# Revit family: QSC TSC-70-G3 Stand
name_source: partatom
category: Communication Devices
revit_build: Autodesk Revit 2018 (Build: 20190510_1515(x64)
units: mm (PartAtom-declared; Revit-internal decimal feet)

## family parameters
Cut with Voids When Loaded = Yes
Host = Face
Maintain Annotation Orientation = No
Part Type = Normal
Room Calculation Point = No
Round Connector Dimension = Use Diameter
Shared = No

## types (1)
- QSC TSC-70-G3 Stand
    Communication Ports = 1 Gbps RJ45 LAN, 1 Type-C USB 3.1 (Future Use)
    Default Elevation = 0.0 mm
    Depth = 39.1 mm
    Description = PoE Touch Screen Controller
    Enclosure Material = Steel, Paint Finish, Dark Gray, Matte
    Face Material = Glossy Black
    Heat Load Active = 26
    Height = 115.0 mm
    Manufacturer = QSC, LLC
    Manufacturer URL = http://www.qsc.com
    Model = TSC-70-G3
    Product Documentation Link = https://www.qsc.com
    Product Page URL = https://www.qsc.com
    Regulatory Compliance = UL, CAN ICES-3 (B)/NMB-3 (B)
    Screen Material = Metal Panel
    Temperature Max = 50° C
    Temperature Min = 0° C
    URL = https://www.qsc.com
    Voltage DC = PoE Class 3
    Weight Product (kg) = 0.564
    Weight Product (lb) = 1.24
    Width = 185.0 mm

## geometry (parser evidence)
native form markers: Sweep x4
no freeform markers — native parametric forms only
